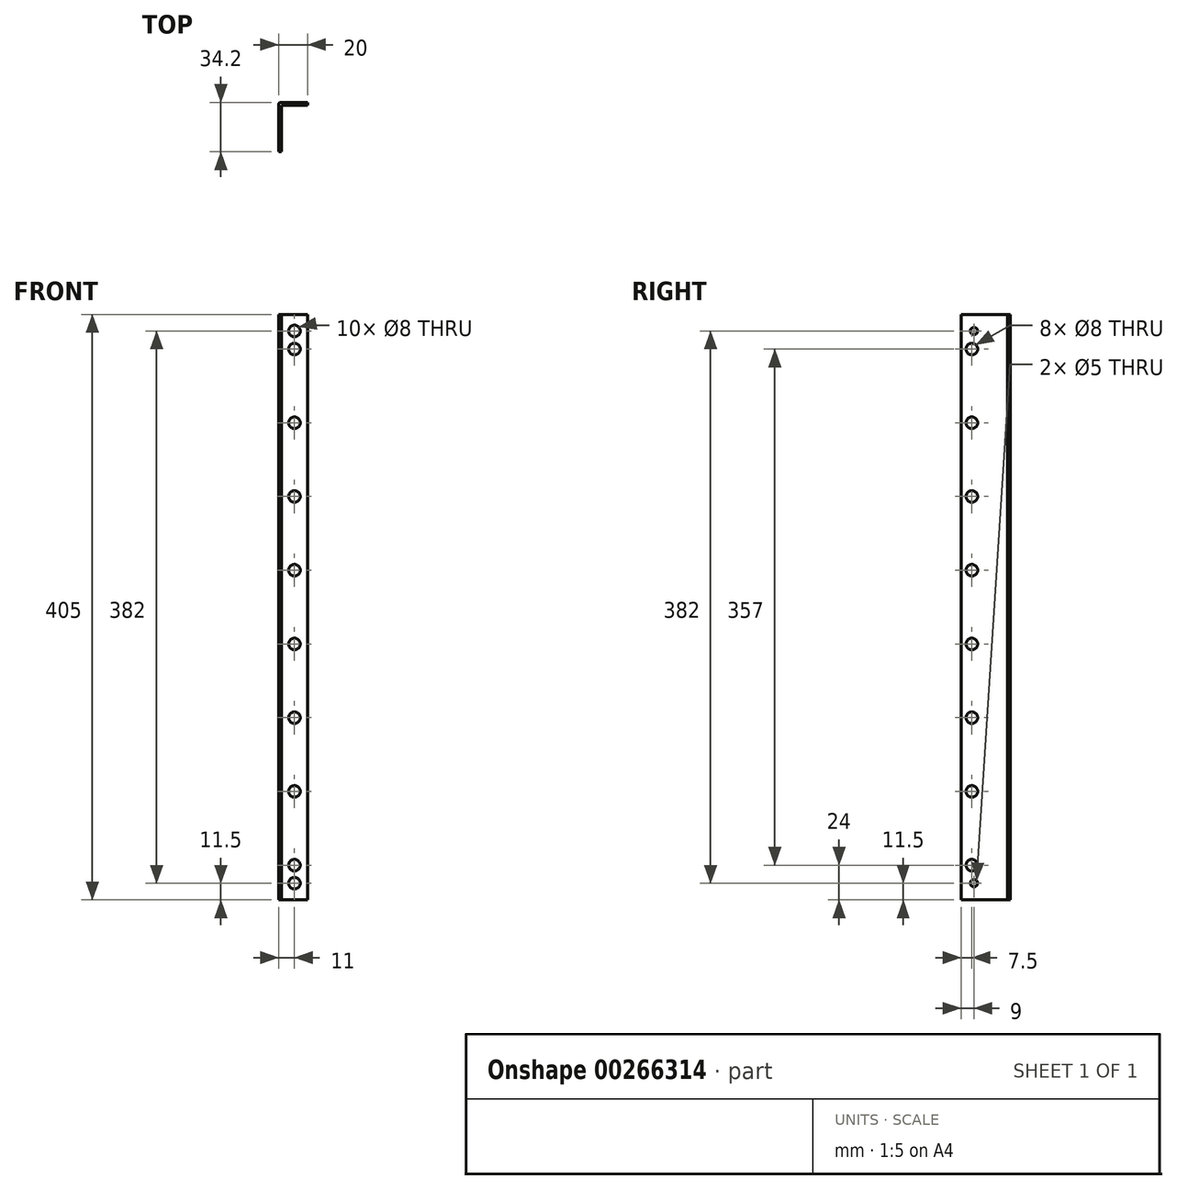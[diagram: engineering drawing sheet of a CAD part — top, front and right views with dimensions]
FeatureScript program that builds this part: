
annotation { "Feature Type Name" : "Feature", "Feature Type Description" : "" }
export const myFeature = defineFeature(function(context is Context, id is Id, definition is map)
    precondition{}
    {
        {
            var Q0;
            Q0=qCreatedBy(makeId("Top.planeOp"),FACE);
            var sketch = newSketch(context, id + "F0", { "sketchPlane" : qUnion([Q0])});
            skLineSegment(sketch, "E0", {"start": v(0, 0) * mm, "end": v(2, 0) * mm});
            skLineSegment(sketch, "E1", {"start": v(2, 0) * mm, "end": v(2, 32.2) * mm});
            skLineSegment(sketch, "E2", {"start": v(2, 32.2) * mm, "end": v(20, 32.2) * mm});
            skLineSegment(sketch, "E3", {"start": v(20, 32.2) * mm, "end": v(20, 34.2) * mm});
            skLineSegment(sketch, "E4", {"start": v(20, 34.2) * mm, "end": v(1.5, 34.2) * mm});
            skLineSegment(sketch, "E5", {"start": v(0, 32.7) * mm, "end": v(0, 0) * mm});
            skPoint(sketch, "E6.visualSharp", {"position": v(0, 34.2) * mm});
            skArc(sketch, "E6.filletArc", {"start": v(1.5, 34.2) * mm, "mid": v(0.44, 33.76) * mm, "end": v(0, 32.7) * mm});
            skSolve(sketch);
        }
        {
            var Q0;
            Q0=makeQuery(id+"F0.imprint","IMPRINT",FACE,{"disambiguationData":[TD([[makeQuery(id+"F0.imprint","IMPRINT",EDGE,{"derivedFrom":sQuery(id+"F0.wireOp",EDGE,"E0")}),1.0]])]});
            extrude(context, id + "F1", {"entities" : qUnion([Q0]), "depth" : 405 * mm});
        }
        {
            var Q0;
            Q0=makeQuery(id+"F1.opExtrude","SWEPT_FACE",FACE,{"disambiguationData":[OSD([sQuery(id+"F0.wireOp",EDGE,"E1")])]});
            var sketch = newSketch(context, id + "F2", { "sketchPlane" : qUnion([Q0])});
            skCircle(sketch, "E7", {"center": v(9, 393.5) * mm, "radius": 2.5 * mm});
            skCircle(sketch, "E8", {"center": v(7.5, 381) * mm, "radius": 4 * mm});
            skCircle(sketch, "E9", {"center": v(7.5, 330) * mm, "radius": 4 * mm});
            skCircle(sketch, "E10", {"center": v(7.5, 24) * mm, "radius": 4 * mm});
            skCircle(sketch, "E11", {"center": v(9, 11.5) * mm, "radius": 2.5 * mm});
            skCircle(sketch, "E12.0.1.0", {"center": v(7.5, 279) * mm, "radius": 4 * mm});
            skCircle(sketch, "E12.0.2.0", {"center": v(7.5, 228) * mm, "radius": 4 * mm});
            skCircle(sketch, "E12.0.3.0", {"center": v(7.5, 177) * mm, "radius": 4 * mm});
            skCircle(sketch, "E12.0.4.0", {"center": v(7.5, 126) * mm, "radius": 4 * mm});
            skCircle(sketch, "E12.0.5.0", {"center": v(7.5, 75) * mm, "radius": 4 * mm});
            skLineSegment(sketch, "E12.direction1", {"start": v(7.5, 330) * mm, "end": v(32.5, 330) * mm, "construction": true});
            skLineSegment(sketch, "E12.direction2", {"start": v(7.5, 330) * mm, "end": v(7.5, 279) * mm, "construction": true});
            skSolve(sketch);
        }
        {
            var Q0;
            Q0=makeQuery(id+"F2.imprint","IMPRINT",FACE,{"disambiguationData":[TD([[makeQuery(id+"F2.imprint","IMPRINT",EDGE,{"derivedFrom":sQuery(id+"F2.wireOp",EDGE,"E7")}),1.0]])]});
            var Q1;
            Q1=makeQuery(id+"F2.imprint","IMPRINT",FACE,{"disambiguationData":[TD([[makeQuery(id+"F2.imprint","IMPRINT",EDGE,{"derivedFrom":sQuery(id+"F2.wireOp",EDGE,"E8")}),1.0]])]});
            var Q2;
            Q2=makeQuery(id+"F2.imprint","IMPRINT",FACE,{"disambiguationData":[TD([[makeQuery(id+"F2.imprint","IMPRINT",EDGE,{"derivedFrom":sQuery(id+"F2.wireOp",EDGE,"E9")}),1.0]])]});
            var Q3;
            Q3=makeQuery(id+"F2.imprint","IMPRINT",FACE,{"disambiguationData":[TD([[makeQuery(id+"F2.imprint","IMPRINT",EDGE,{"derivedFrom":sQuery(id+"F2.wireOp",EDGE,"E12.0.1.0")}),1.0]])]});
            var Q4;
            Q4=makeQuery(id+"F2.imprint","IMPRINT",FACE,{"disambiguationData":[TD([[makeQuery(id+"F2.imprint","IMPRINT",EDGE,{"derivedFrom":sQuery(id+"F2.wireOp",EDGE,"E12.0.2.0")}),1.0]])]});
            var Q5;
            Q5=makeQuery(id+"F2.imprint","IMPRINT",FACE,{"disambiguationData":[TD([[makeQuery(id+"F2.imprint","IMPRINT",EDGE,{"derivedFrom":sQuery(id+"F2.wireOp",EDGE,"E12.0.3.0")}),1.0]])]});
            var Q6;
            Q6=makeQuery(id+"F2.imprint","IMPRINT",FACE,{"disambiguationData":[TD([[makeQuery(id+"F2.imprint","IMPRINT",EDGE,{"derivedFrom":sQuery(id+"F2.wireOp",EDGE,"E12.0.4.0")}),1.0]])]});
            var Q7;
            Q7=makeQuery(id+"F2.imprint","IMPRINT",FACE,{"disambiguationData":[TD([[makeQuery(id+"F2.imprint","IMPRINT",EDGE,{"derivedFrom":sQuery(id+"F2.wireOp",EDGE,"E12.0.5.0")}),1.0]])]});
            var Q8;
            Q8=makeQuery(id+"F2.imprint","IMPRINT",FACE,{"disambiguationData":[TD([[makeQuery(id+"F2.imprint","IMPRINT",EDGE,{"derivedFrom":sQuery(id+"F2.wireOp",EDGE,"E10")}),1.0]])]});
            var Q9;
            Q9=makeQuery(id+"F2.imprint","IMPRINT",FACE,{"disambiguationData":[TD([[makeQuery(id+"F2.imprint","IMPRINT",EDGE,{"derivedFrom":sQuery(id+"F2.wireOp",EDGE,"E11")}),1.0]])]});
            var Q10;
            Q10=sQuery(id+"F2.wireOp",EDGE,"E9");
            var Q11;
            Q11=sQuery(id+"F2.wireOp",EDGE,"E8");
            var Q12;
            Q12=sQuery(id+"F2.wireOp",EDGE,"E7");
            var Q13;
            Q13=sQuery(id+"F2.wireOp",EDGE,"E12.0.1.0");
            var Q14;
            Q14=sQuery(id+"F2.wireOp",EDGE,"E12.0.2.0");
            var Q15;
            Q15=sQuery(id+"F2.wireOp",EDGE,"E12.0.3.0");
            var Q16;
            Q16=sQuery(id+"F2.wireOp",EDGE,"E12.0.4.0");
            var Q17;
            Q17=sQuery(id+"F2.wireOp",EDGE,"E12.0.5.0");
            var Q18;
            Q18=sQuery(id+"F2.wireOp",EDGE,"E10");
            var Q19;
            Q19=sQuery(id+"F2.wireOp",EDGE,"E11");
            extrude(context, id + "F3", {"entities" : qUnion([Q0, Q1, Q2, Q3, Q4, Q5, Q6, Q7, Q8, Q9]), "operationType" : NewBodyOperationType.REMOVE, "surfaceEntities" : qUnion([Q10, Q11, Q12, Q13, Q14, Q15, Q16, Q17, Q18, Q19]), "endBound" : BoundingType.THROUGH_ALL, "oppositeDirection" : true, "depth" : 25 * mm});
        }
        {
            var Q0;
            Q0=makeQuery(id+"F1.opExtrude","SWEPT_FACE",FACE,{"disambiguationData":[OSD([sQuery(id+"F0.wireOp",EDGE,"E2")])]});
            var sketch = newSketch(context, id + "F4", { "sketchPlane" : qUnion([Q0])});
            skCircle(sketch, "E13", {"center": v(11, 393.5) * mm, "radius": 4 * mm});
            skPoint(sketch, "E13.centerSnap0", {"position": v(11, 405) * mm});
            skCircle(sketch, "E14", {"center": v(11, 381) * mm, "radius": 4 * mm});
            skCircle(sketch, "E15.0.1.0", {"center": v(11, 330) * mm, "radius": 4 * mm});
            skCircle(sketch, "E15.0.2.0", {"center": v(11, 279) * mm, "radius": 4 * mm});
            skCircle(sketch, "E15.0.3.0", {"center": v(11, 228) * mm, "radius": 4 * mm});
            skCircle(sketch, "E15.0.4.0", {"center": v(11, 177) * mm, "radius": 4 * mm});
            skCircle(sketch, "E15.0.5.0", {"center": v(11, 126) * mm, "radius": 4 * mm});
            skCircle(sketch, "E15.0.6.0", {"center": v(11, 75) * mm, "radius": 4 * mm});
            skCircle(sketch, "E15.0.7.0", {"center": v(11, 24) * mm, "radius": 4 * mm});
            skLineSegment(sketch, "E15.direction1", {"start": v(11, 381) * mm, "end": v(62, 381) * mm, "construction": true});
            skLineSegment(sketch, "E15.direction2", {"start": v(11, 381) * mm, "end": v(11, 330) * mm, "construction": true});
            skCircle(sketch, "E16.0.1.0", {"center": v(11, 11.5) * mm, "radius": 4 * mm});
            skLineSegment(sketch, "E16.direction1", {"start": v(11, 393.5) * mm, "end": v(36, 393.5) * mm, "construction": true});
            skLineSegment(sketch, "E16.direction2", {"start": v(11, 393.5) * mm, "end": v(11, 11.5) * mm, "construction": true});
            skSolve(sketch);
        }
        {
            var Q0;
            Q0=makeQuery(id+"F4.imprint","IMPRINT",FACE,{"disambiguationData":[TD([[makeQuery(id+"F4.imprint","IMPRINT",EDGE,{"derivedFrom":sQuery(id+"F4.wireOp",EDGE,"E13")}),1.0]])]});
            var Q1;
            Q1=makeQuery(id+"F4.imprint","IMPRINT",FACE,{"disambiguationData":[TD([[makeQuery(id+"F4.imprint","IMPRINT",EDGE,{"derivedFrom":sQuery(id+"F4.wireOp",EDGE,"E14")}),1.0]])]});
            var Q2;
            Q2=makeQuery(id+"F4.imprint","IMPRINT",FACE,{"disambiguationData":[TD([[makeQuery(id+"F4.imprint","IMPRINT",EDGE,{"derivedFrom":sQuery(id+"F4.wireOp",EDGE,"E15.0.1.0")}),1.0]])]});
            var Q3;
            Q3=makeQuery(id+"F4.imprint","IMPRINT",FACE,{"disambiguationData":[TD([[makeQuery(id+"F4.imprint","IMPRINT",EDGE,{"derivedFrom":sQuery(id+"F4.wireOp",EDGE,"E15.0.2.0")}),1.0]])]});
            var Q4;
            Q4=makeQuery(id+"F4.imprint","IMPRINT",FACE,{"disambiguationData":[TD([[makeQuery(id+"F4.imprint","IMPRINT",EDGE,{"derivedFrom":sQuery(id+"F4.wireOp",EDGE,"E15.0.3.0")}),1.0]])]});
            var Q5;
            Q5=makeQuery(id+"F4.imprint","IMPRINT",FACE,{"disambiguationData":[TD([[makeQuery(id+"F4.imprint","IMPRINT",EDGE,{"derivedFrom":sQuery(id+"F4.wireOp",EDGE,"E15.0.4.0")}),1.0]])]});
            var Q6;
            Q6=makeQuery(id+"F4.imprint","IMPRINT",FACE,{"disambiguationData":[TD([[makeQuery(id+"F4.imprint","IMPRINT",EDGE,{"derivedFrom":sQuery(id+"F4.wireOp",EDGE,"E15.0.5.0")}),1.0]])]});
            var Q7;
            Q7=makeQuery(id+"F4.imprint","IMPRINT",FACE,{"disambiguationData":[TD([[makeQuery(id+"F4.imprint","IMPRINT",EDGE,{"derivedFrom":sQuery(id+"F4.wireOp",EDGE,"E15.0.6.0")}),1.0]])]});
            var Q8;
            Q8=makeQuery(id+"F4.imprint","IMPRINT",FACE,{"disambiguationData":[TD([[makeQuery(id+"F4.imprint","IMPRINT",EDGE,{"derivedFrom":sQuery(id+"F4.wireOp",EDGE,"E16.0.1.0")}),1.0]])]});
            var Q9;
            Q9=makeQuery(id+"F4.imprint","IMPRINT",FACE,{"disambiguationData":[TD([[makeQuery(id+"F4.imprint","IMPRINT",EDGE,{"derivedFrom":sQuery(id+"F4.wireOp",EDGE,"E15.0.7.0")}),1.0]])]});
            var Q10;
            Q10=sQuery(id+"F4.wireOp",EDGE,"E13");
            var Q11;
            Q11=sQuery(id+"F4.wireOp",EDGE,"E14");
            var Q12;
            Q12=sQuery(id+"F4.wireOp",EDGE,"E15.0.1.0");
            var Q13;
            Q13=sQuery(id+"F4.wireOp",EDGE,"E15.0.2.0");
            var Q14;
            Q14=sQuery(id+"F4.wireOp",EDGE,"E15.0.3.0");
            var Q15;
            Q15=sQuery(id+"F4.wireOp",EDGE,"E15.0.4.0");
            var Q16;
            Q16=sQuery(id+"F4.wireOp",EDGE,"E15.0.5.0");
            var Q17;
            Q17=sQuery(id+"F4.wireOp",EDGE,"E15.0.6.0");
            var Q18;
            Q18=sQuery(id+"F4.wireOp",EDGE,"E15.0.7.0");
            var Q19;
            Q19=sQuery(id+"F4.wireOp",EDGE,"E16.0.1.0");
            extrude(context, id + "F5", {"entities" : qUnion([Q0, Q1, Q2, Q3, Q4, Q5, Q6, Q7, Q8, Q9]), "operationType" : NewBodyOperationType.REMOVE, "surfaceEntities" : qUnion([Q10, Q11, Q12, Q13, Q14, Q15, Q16, Q17, Q18, Q19]), "endBound" : BoundingType.THROUGH_ALL, "oppositeDirection" : true, "depth" : 25 * mm});
        }
    });
